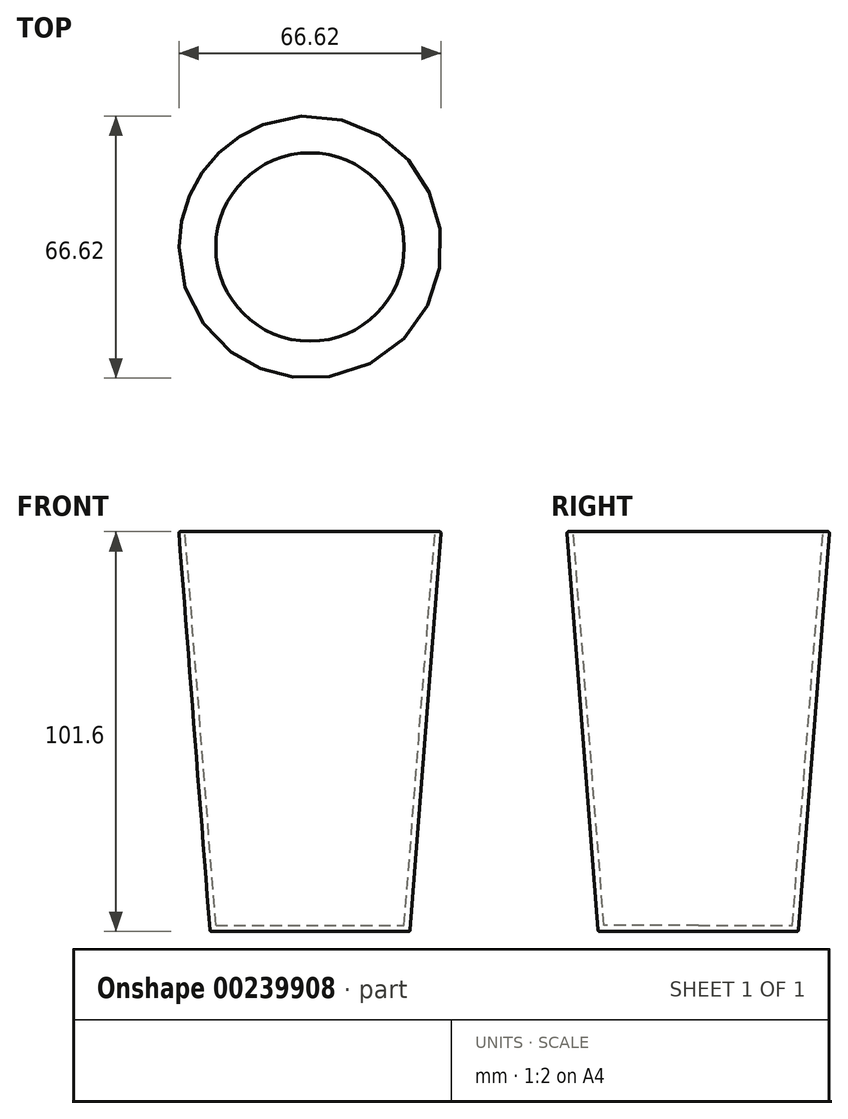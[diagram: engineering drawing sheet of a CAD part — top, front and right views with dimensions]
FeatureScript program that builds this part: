
annotation { "Feature Type Name" : "Feature", "Feature Type Description" : "" }
export const myFeature = defineFeature(function(context is Context, id is Id, definition is map)
    precondition{}
    {
        {
            var Q0;
            Q0=qCreatedBy(makeId("Front.planeOp"),FACE);
            var sketch = newSketch(context, id + "F0", { "sketchPlane" : qUnion([Q0])});
            skLineSegment(sketch, "E0", {"start": v(0, 0) * mm, "end": v(0, 101.6) * mm});
            skLineSegment(sketch, "E1", {"start": v(0, 101.6) * mm, "end": v(33.34, 101.6) * mm});
            skLineSegment(sketch, "E2", {"start": v(33.34, 101.6) * mm, "end": v(25.4, 0) * mm});
            skLineSegment(sketch, "E3", {"start": v(25.4, 0) * mm, "end": v(0, 0) * mm});
            skPoint(sketch, "E4", {"position": v(31.75, 101.6) * mm});
            skPoint(sketch, "E5", {"position": v(0, 1.59) * mm});
            skLineSegment(sketch, "E6", {"start": v(31.75, 101.6) * mm, "end": v(23.94, 1.59) * mm});
            skLineSegment(sketch, "E7", {"start": v(23.94, 1.59) * mm, "end": v(0, 1.59) * mm});
            skSolve(sketch);
        }
        {
            var Q0;
            {var subQ1=sQuery(id+"F0.wireOp",EDGE,"E2");Q0=makeQuery(id+"F0.imprint","IMPRINT",FACE,{"disambiguationData":[TD([[makeQuery(id+"F0.imprint","IMPRINT",EDGE,{"derivedFrom":subQ1}),-1.0]])]});}
            var Q1;
            Q1=sQuery(id+"F0.wireOp",EDGE,"E0");
            revolve(context, id + "F1", {"entities" : qUnion([Q0]), "axis" : qUnion([Q1]), "revolveType" : RevolveType.FULL});
        }
        {
            var Q0;
            Q0=makeQuery(id+"F1.opRevolve","SWEPT_EDGE",EDGE,{"disambiguationData":[OSD([sQuery(id+"F0.wireOp",EDGE,"E1"),sQuery(id+"F0.wireOp",EDGE,"E2")])]});
            fillet(context, id + "F2", {"entities" : qUnion([Q0]), "radius" : 0.4 * mm, "tangentPropagation" : true, "allowEdgeOverflow" : false});
        }
        {
            var Q0;
            Q0=makeQuery(id+"F1.opRevolve","SWEPT_EDGE",EDGE,{"disambiguationData":[OSD([sQuery(id+"F0.wireOp",EDGE,"E1"),sQuery(id+"F0.wireOp",EDGE,"E6")])]});
            fillet(context, id + "F3", {"entities" : qUnion([Q0]), "radius" : 0.4 * mm, "tangentPropagation" : true, "allowEdgeOverflow" : false});
        }
        {
            var Q0;
            Q0=makeQuery(id+"F1.opRevolve","SWEPT_EDGE",EDGE,{"disambiguationData":[OSD([sQuery(id+"F0.wireOp",EDGE,"E2"),sQuery(id+"F0.wireOp",EDGE,"E3")])]});
            fillet(context, id + "F4", {"entities" : qUnion([Q0]), "radius" : 0.4 * mm, "tangentPropagation" : true, "allowEdgeOverflow" : false});
        }
    });
